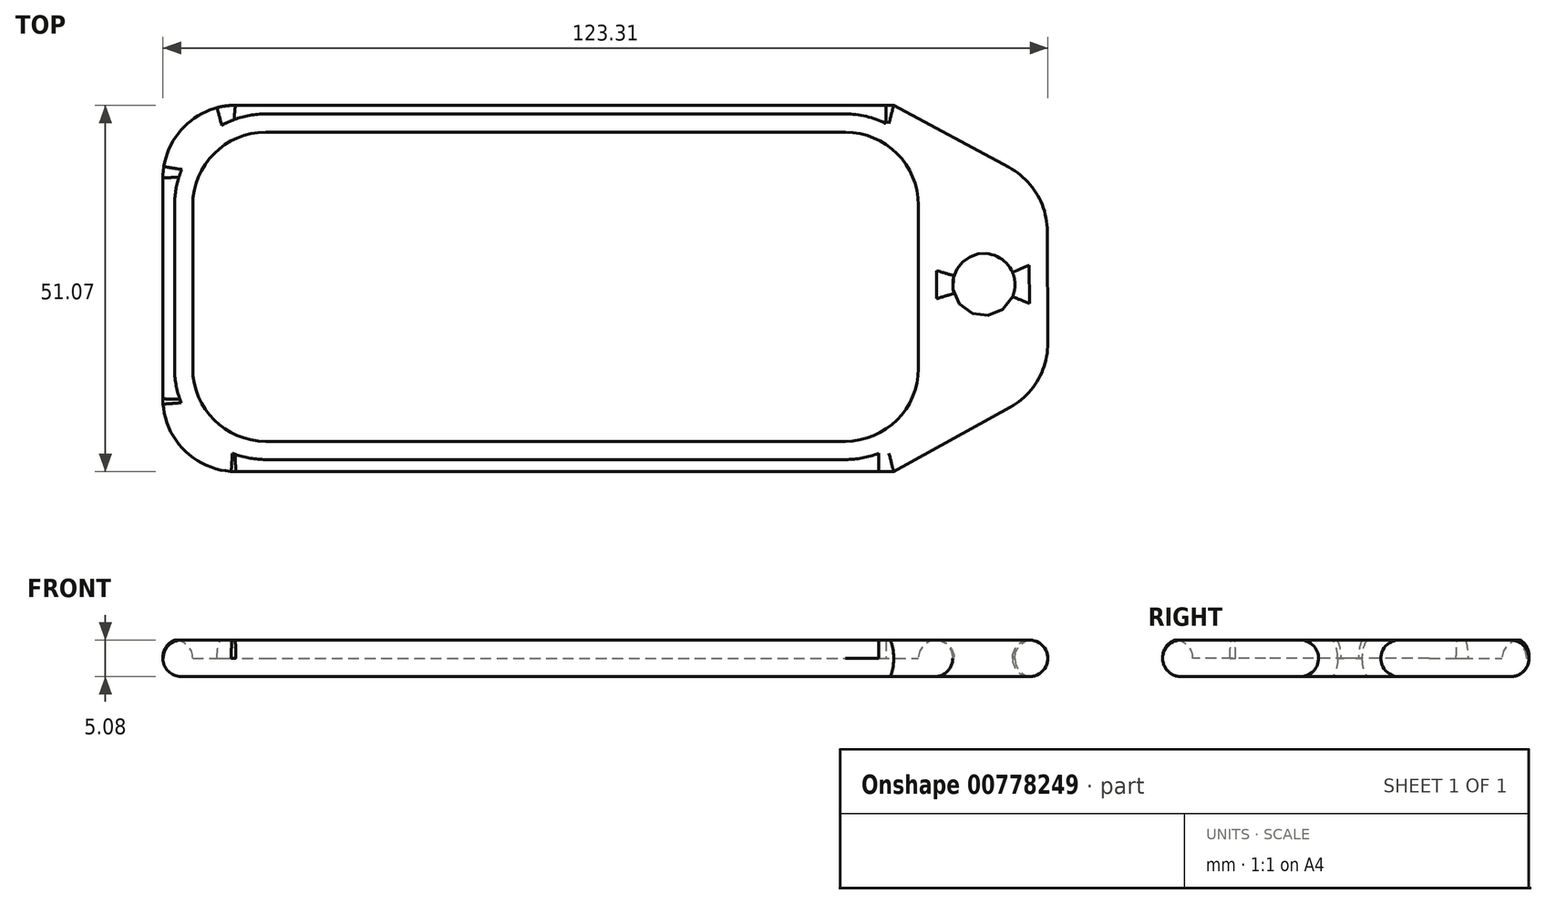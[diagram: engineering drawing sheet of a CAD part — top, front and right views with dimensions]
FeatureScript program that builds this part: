
annotation { "Feature Type Name" : "Feature", "Feature Type Description" : "" }
export const myFeature = defineFeature(function(context is Context, id is Id, definition is map)
    precondition{}
    {
        {
            var Q0;
            Q0=qCreatedBy(makeId("Top.planeOp"),FACE);
            var sketch = newSketch(context, id + "F0", { "sketchPlane" : qUnion([Q0])});
            skLineSegment(sketch, "E0.bottom", {"start": v(-56.17, 44.44) * mm, "end": v(35.5, 44.44) * mm});
            skLineSegment(sketch, "E0.top", {"start": v(-56.17, -6.63) * mm, "end": v(35.5, -6.63) * mm});
            skLineSegment(sketch, "E0.left", {"start": v(-66.33, 34.28) * mm, "end": v(-66.33, 3.53) * mm});
            skLineSegment(sketch, "E0.right", {"start": v(35.5, 44.44) * mm, "end": v(35.5, -6.63) * mm});
            skLineSegment(sketch, "E1", {"start": v(35.5, 44.44) * mm, "end": v(51.57, 35.76) * mm});
            skLineSegment(sketch, "E2", {"start": v(35.5, -6.63) * mm, "end": v(51.73, 2.34) * mm});
            skLineSegment(sketch, "E3", {"start": v(56.98, 11.28) * mm, "end": v(56.9, 26.87) * mm});
            skPoint(sketch, "E4.visualSharp", {"position": v(56.88, 32.9) * mm});
            skArc(sketch, "E4.filletArc", {"start": v(56.9, 26.87) * mm, "mid": v(55.46, 32.05) * mm, "end": v(51.57, 35.76) * mm});
            skPoint(sketch, "E5.visualSharp", {"position": v(57, 5.26) * mm});
            skArc(sketch, "E5.filletArc", {"start": v(51.73, 2.34) * mm, "mid": v(55.58, 6.1) * mm, "end": v(56.98, 11.28) * mm});
            skPoint(sketch, "E6.visualSharp", {"position": v(-66.33, 44.44) * mm});
            skArc(sketch, "E6.filletArc", {"start": v(-56.17, 44.44) * mm, "mid": v(-63.36, 41.46) * mm, "end": v(-66.33, 34.28) * mm});
            skPoint(sketch, "E7.visualSharp", {"position": v(-66.33, -6.63) * mm});
            skArc(sketch, "E7.filletArc", {"start": v(-66.33, 3.53) * mm, "mid": v(-63.36, -3.65) * mm, "end": v(-56.17, -6.63) * mm});
            skSolve(sketch);
        }
        {
            var Q0;
            Q0 = qSketchRegion(id + "F0", true);
            extrude(context, id + "F1", {"entities" : qUnion([Q0]), "depth" : 5.08 * mm, "offsetDistance" : 25.4 * mm});
        }
        {
            var Q0;
            Q0=qCreatedBy(makeId("Top.planeOp"),FACE);
            var sketch = newSketch(context, id + "F2", { "sketchPlane" : qUnion([Q0])});
            skLineSegment(sketch, "E8.bottom", {"start": v(-52, 40.68) * mm, "end": v(28.78, 40.68) * mm});
            skLineSegment(sketch, "E8.top", {"start": v(-52, -2.41) * mm, "end": v(28.78, -2.41) * mm});
            skLineSegment(sketch, "E8.left", {"start": v(-62.17, 30.52) * mm, "end": v(-62.17, 7.75) * mm});
            skLineSegment(sketch, "E8.right", {"start": v(38.94, 30.52) * mm, "end": v(38.94, 7.75) * mm});
            skPoint(sketch, "E9.visualSharp", {"position": v(-62.17, 40.68) * mm});
            skArc(sketch, "E9.filletArc", {"start": v(-52, 40.68) * mm, "mid": v(-59.2, 37.7) * mm, "end": v(-62.17, 30.52) * mm});
            skPoint(sketch, "E10.visualSharp", {"position": v(-62.17, -2.41) * mm});
            skArc(sketch, "E10.filletArc", {"start": v(-62.17, 7.75) * mm, "mid": v(-59.2, 0.56) * mm, "end": v(-52, -2.41) * mm});
            skPoint(sketch, "E11.visualSharp", {"position": v(38.94, -2.41) * mm});
            skArc(sketch, "E11.filletArc", {"start": v(28.78, -2.41) * mm, "mid": v(35.97, 0.56) * mm, "end": v(38.94, 7.75) * mm});
            skPoint(sketch, "E12.visualSharp", {"position": v(38.94, 40.68) * mm});
            skArc(sketch, "E12.filletArc", {"start": v(38.94, 30.52) * mm, "mid": v(35.97, 37.7) * mm, "end": v(28.78, 40.68) * mm});
            skSolve(sketch);
        }
        {
            var Q0;
            Q0 = qSketchRegion(id + "F2", true);
            extrude(context, id + "F3", {"entities" : qUnion([Q0]), "operationType" : NewBodyOperationType.REMOVE, "depth" : 31.24 * mm, "offsetDistance" : 25.4 * mm, "hasSecondDirection" : true, "secondDirectionOppositeDirection" : false, "secondDirectionDepth" : 2.54 * mm});
        }
        {
            var Q0;
            Q0=makeQuery(id+"F3.boolean.opBoolean","INTERSECT",EDGE,{"derivedFrom":[makeQuery(id+"F1.opExtrude","CAP_FACE",FACE,{"disambiguationData":[OSD([sQuery(id+"F0.wireOp",EDGE,"E0.bottom"),sQuery(id+"F0.wireOp",EDGE,"E0.top"),sQuery(id+"F0.wireOp",EDGE,"E0.left"),sQuery(id+"F0.wireOp",EDGE,"E1"),sQuery(id+"F0.wireOp",EDGE,"E2"),sQuery(id+"F0.wireOp",EDGE,"E3"),sQuery(id+"F0.wireOp",EDGE,"E4.filletArc"),sQuery(id+"F0.wireOp",EDGE,"E5.filletArc"),sQuery(id+"F0.wireOp",EDGE,"E6.filletArc"),sQuery(id+"F0.wireOp",EDGE,"E7.filletArc")])],"isStart":false}),makeQuery(id+"F3.opExtrude","SWEPT_FACE",FACE,{"disambiguationData":[OSD([sQuery(id+"F2.wireOp",EDGE,"E8.bottom")])]})]});
            fillet(context, id + "F4", {"entities" : qUnion([Q0]), "radius" : 2.54 * mm, "tangentPropagation" : true, "allowEdgeOverflow" : false});
        }
        {
            var Q0;
            Q0=makeQuery(id+"F1.opExtrude","CAP_EDGE",EDGE,{"disambiguationData":[OSD([sQuery(id+"F0.wireOp",EDGE,"E0.top")])],"isStart":true});
            var Q1;
            Q1=makeQuery(id+"F1.opExtrude","CAP_EDGE",EDGE,{"disambiguationData":[OSD([sQuery(id+"F0.wireOp",EDGE,"E5.filletArc")])],"isStart":true});
            fillet(context, id + "F5", {"entities" : qUnion([Q0, Q1]), "radius" : 2.54 * mm, "tangentPropagation" : true, "allowEdgeOverflow" : false});
        }
        {
            var Q0;
            {var subQ0=sQuery(id+"F0.wireOp",EDGE,"E3");Q0=makeQuery(id+"F5.opFillet","BLEND_EDGE",EDGE,{"blendedFrom":[makeQuery(id+"F1.opExtrude","CAP_EDGE",EDGE,{"disambiguationData":[OSD([subQ0])],"isStart":true}),makeQuery(id+"F1.opExtrude","SWEPT_FACE",FACE,{"disambiguationData":[OSD([subQ0])]})],"blendedInto":[makeQuery(id+"F1.opExtrude","SWEPT_FACE",FACE,{"disambiguationData":[OSD([subQ0])]})]});}
            var Q1;
            Q1=makeQuery(id+"F1.opExtrude","CAP_EDGE",EDGE,{"disambiguationData":[OSD([sQuery(id+"F0.wireOp",EDGE,"E3")])],"isStart":false});
            var Q2;
            Q2=makeQuery(id+"F1.opExtrude","CAP_EDGE",EDGE,{"disambiguationData":[OSD([sQuery(id+"F0.wireOp",EDGE,"E7.filletArc")])],"isStart":false});
            fillet(context, id + "F6", {"entities" : qUnion([Q0, Q1, Q2]), "radius" : 2.54 * mm, "tangentPropagation" : true, "allowEdgeOverflow" : false});
        }
        {
            var Q0;
            Q0=qCreatedBy(makeId("Top.planeOp"),FACE);
            var sketch = newSketch(context, id + "F7", { "sketchPlane" : qUnion([Q0])});
            skCircle(sketch, "E13", {"center": v(48.07, 19.43) * mm, "radius": 4.33 * mm});
            skSolve(sketch);
        }
        {
            var Q0;
            Q0 = qSketchRegion(id + "F7", true);
            extrude(context, id + "F8", {"entities" : qUnion([Q0]), "operationType" : NewBodyOperationType.REMOVE, "oppositeDirection" : true, "depth" : 76.2 * mm, "offsetDistance" : 25.4 * mm, "hasSecondDirection" : true, "secondDirectionOppositeDirection" : false, "secondDirectionDepth" : 76.2 * mm});
        }
        {
            var Q0;
            Q0=makeQuery(id+"F8.boolean.opBoolean","INTERSECT",EDGE,{"derivedFrom":[makeQuery(id+"F1.opExtrude","CAP_FACE",FACE,{"disambiguationData":[OSD([sQuery(id+"F0.wireOp",EDGE,"E0.bottom"),sQuery(id+"F0.wireOp",EDGE,"E0.top"),sQuery(id+"F0.wireOp",EDGE,"E0.left"),sQuery(id+"F0.wireOp",EDGE,"E1"),sQuery(id+"F0.wireOp",EDGE,"E2"),sQuery(id+"F0.wireOp",EDGE,"E3"),sQuery(id+"F0.wireOp",EDGE,"E4.filletArc"),sQuery(id+"F0.wireOp",EDGE,"E5.filletArc"),sQuery(id+"F0.wireOp",EDGE,"E6.filletArc"),sQuery(id+"F0.wireOp",EDGE,"E7.filletArc")])],"isStart":true}),makeQuery(id+"F8.opExtrude","SWEPT_FACE",FACE,{"disambiguationData":[OSD([sQuery(id+"F7.wireOp",EDGE,"E13")])]})]});
            var Q1;
            Q1=makeQuery(id+"F8.boolean.opBoolean","INTERSECT",EDGE,{"derivedFrom":[makeQuery(id+"F6.opFillet","SPLIT",FACE,{"disambiguationData":[OD(0.0)],"derivedFrom":makeQuery(id+"F1.opExtrude","CAP_FACE",FACE,{"disambiguationData":[OSD([sQuery(id+"F0.wireOp",EDGE,"E0.bottom"),sQuery(id+"F0.wireOp",EDGE,"E0.top"),sQuery(id+"F0.wireOp",EDGE,"E0.left"),sQuery(id+"F0.wireOp",EDGE,"E1"),sQuery(id+"F0.wireOp",EDGE,"E2"),sQuery(id+"F0.wireOp",EDGE,"E3"),sQuery(id+"F0.wireOp",EDGE,"E4.filletArc"),sQuery(id+"F0.wireOp",EDGE,"E5.filletArc"),sQuery(id+"F0.wireOp",EDGE,"E6.filletArc"),sQuery(id+"F0.wireOp",EDGE,"E7.filletArc")])],"isStart":false})}),makeQuery(id+"F8.opExtrude","SWEPT_FACE",FACE,{"disambiguationData":[OSD([sQuery(id+"F7.wireOp",EDGE,"E13")])]})]});
            fillet(context, id + "F9", {"entities" : qUnion([Q0, Q1]), "radius" : 2.54 * mm, "tangentPropagation" : true, "allowEdgeOverflow" : false});
        }
    });
